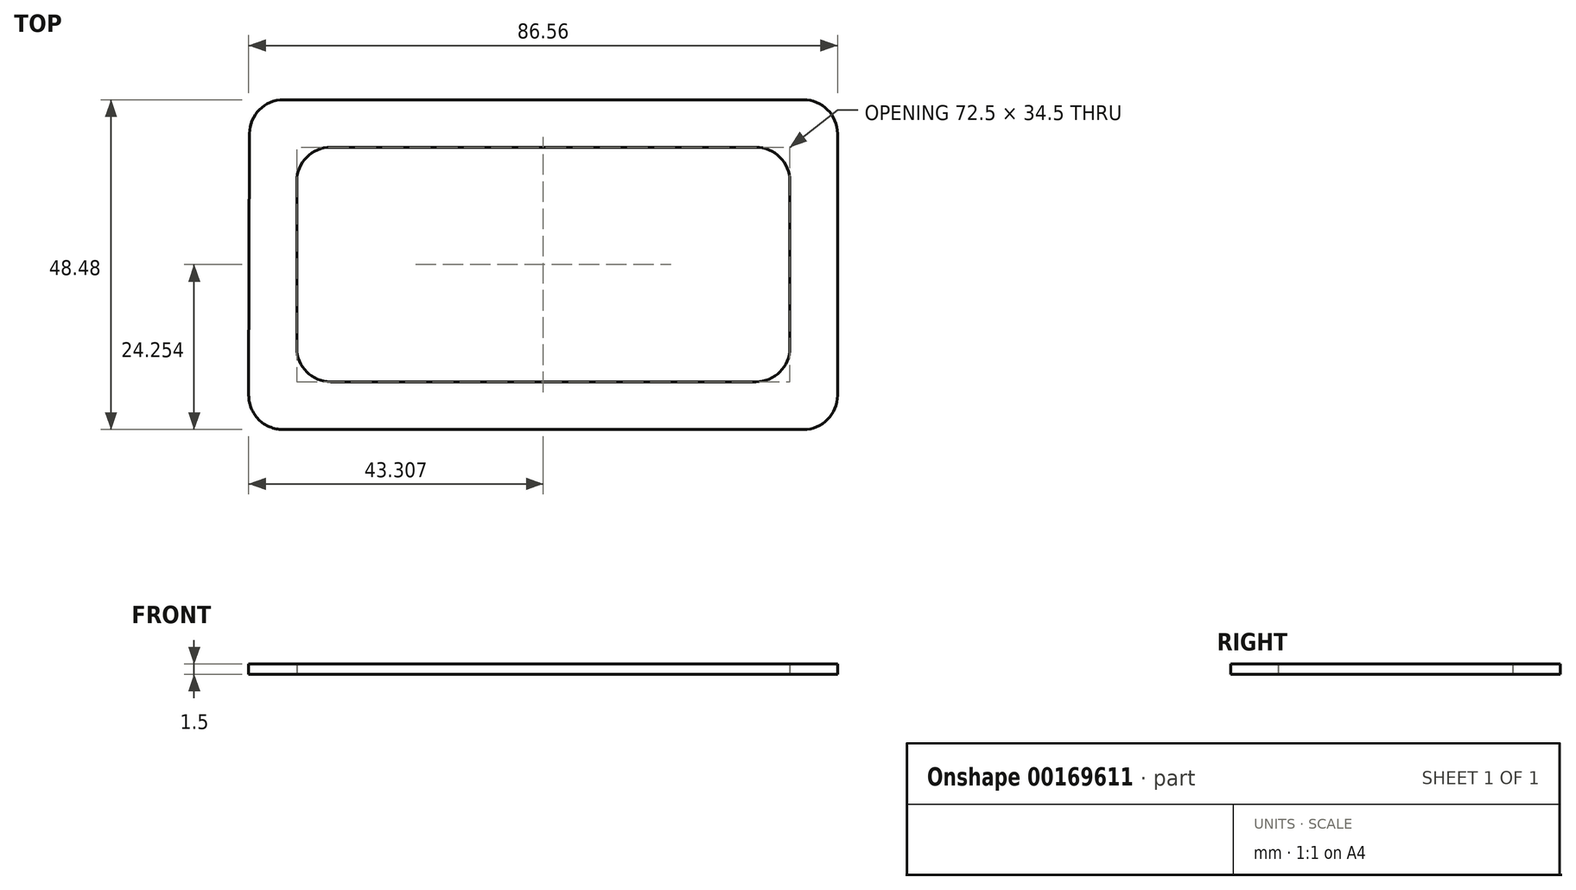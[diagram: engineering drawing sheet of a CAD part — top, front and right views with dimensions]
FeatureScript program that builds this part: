
annotation { "Feature Type Name" : "Feature", "Feature Type Description" : "" }
export const myFeature = defineFeature(function(context is Context, id is Id, definition is map)
    precondition{}
    {
        {
            var Q0;
            Q0=qCreatedBy(makeId("Top.planeOp"),FACE);
            var sketch = newSketch(context, id + "F0", { "sketchPlane" : qUnion([Q0])});
            skLineSegment(sketch, "E0.bottom", {"start": v(12.07, 21.8) * mm, "end": v(74.57, 21.8) * mm});
            skLineSegment(sketch, "E0.top", {"start": v(12.07, -12.7) * mm, "end": v(74.57, -12.7) * mm});
            skLineSegment(sketch, "E0.left", {"start": v(7.07, 16.8) * mm, "end": v(7.07, -7.7) * mm});
            skLineSegment(sketch, "E0.right", {"start": v(79.57, 16.8) * mm, "end": v(79.57, -7.7) * mm});
            skPoint(sketch, "E1.visualSharp", {"position": v(7.07, 21.8) * mm});
            skArc(sketch, "E1.filletArc", {"start": v(12.07, 21.8) * mm, "mid": v(8.53, 20.33) * mm, "end": v(7.07, 16.8) * mm});
            skPoint(sketch, "E2.visualSharp", {"position": v(7.07, -12.7) * mm});
            skArc(sketch, "E2.filletArc", {"start": v(7.07, -7.7) * mm, "mid": v(8.53, -11.24) * mm, "end": v(12.07, -12.7) * mm});
            skPoint(sketch, "E3.visualSharp", {"position": v(79.57, -12.7) * mm});
            skArc(sketch, "E3.filletArc", {"start": v(74.57, -12.7) * mm, "mid": v(78.1, -11.24) * mm, "end": v(79.57, -7.7) * mm});
            skPoint(sketch, "E4.visualSharp", {"position": v(79.57, 21.8) * mm});
            skArc(sketch, "E4.filletArc", {"start": v(79.57, 16.8) * mm, "mid": v(78.1, 20.33) * mm, "end": v(74.57, 21.8) * mm});
            skLineSegment(sketch, "E5", {"start": v(7.07, 4.54) * mm, "end": v(0.07, 4.54) * mm, "construction": true});
            skPoint(sketch, "E6.endSnap0", {"position": v(79.57, 4.54) * mm});
            skLineSegment(sketch, "E7.bottom", {"start": v(5.01, -19.7) * mm, "end": v(81.57, -19.7) * mm});
            skLineSegment(sketch, "E7.top", {"start": v(5.12, 28.77) * mm, "end": v(81.57, 28.77) * mm});
            skLineSegment(sketch, "E7.left", {"start": v(0.01, -14.7) * mm, "end": v(0.12, 23.78) * mm});
            skLineSegment(sketch, "E7.right", {"start": v(86.57, -14.7) * mm, "end": v(86.57, 23.77) * mm});
            skPoint(sketch, "E8.visualSharp", {"position": v(0.13, 28.77) * mm});
            skArc(sketch, "E8.filletArc", {"start": v(5.12, 28.77) * mm, "mid": v(1.59, 27.3) * mm, "end": v(0.12, 23.78) * mm});
            skPoint(sketch, "E9.visualSharp", {"position": v(86.57, 28.77) * mm});
            skArc(sketch, "E9.filletArc", {"start": v(86.57, 23.77) * mm, "mid": v(85.1, 27.3) * mm, "end": v(81.57, 28.77) * mm});
            skPoint(sketch, "E10.visualSharp", {"position": v(86.57, -19.7) * mm});
            skArc(sketch, "E10.filletArc", {"start": v(81.57, -19.7) * mm, "mid": v(85.1, -18.24) * mm, "end": v(86.57, -14.7) * mm});
            skPoint(sketch, "E11.visualSharp", {"position": v(0, -19.7) * mm});
            skArc(sketch, "E11.filletArc", {"start": v(0.01, -14.7) * mm, "mid": v(1.47, -18.24) * mm, "end": v(5.01, -19.7) * mm});
            skPoint(sketch, "E12.startSnap0", {"position": v(43.34, 28.77) * mm});
            skPoint(sketch, "E12.endSnap0", {"position": v(43.32, 21.8) * mm});
            skLineSegment(sketch, "E13", {"start": v(79.57, 4.54) * mm, "end": v(86.57, 4.54) * mm, "construction": true});
            skLineSegment(sketch, "E14", {"start": v(43.32, -12.7) * mm, "end": v(43.32, -19.7) * mm, "construction": true});
            skLineSegment(sketch, "E15", {"start": v(79.57, 16.8) * mm, "end": v(86.57, 16.8) * mm, "construction": true});
            skLineSegment(sketch, "E16", {"start": v(79.57, -7.7) * mm, "end": v(86.57, -7.7) * mm, "construction": true});
            skSolve(sketch);
        }
        {
            var Q0;
            Q0=makeQuery(id+"F0.imprint","IMPRINT",FACE,{"disambiguationData":[TD([[makeQuery(id+"F0.imprint","IMPRINT",EDGE,{"derivedFrom":sQuery(id+"F0.wireOp",EDGE,"E0.bottom")}),1.0]])]});
            extrude(context, id + "F1", {"entities" : qUnion([Q0]), "depth" : 1.5 * mm, "offsetDistance" : 25 * mm});
        }
    });
